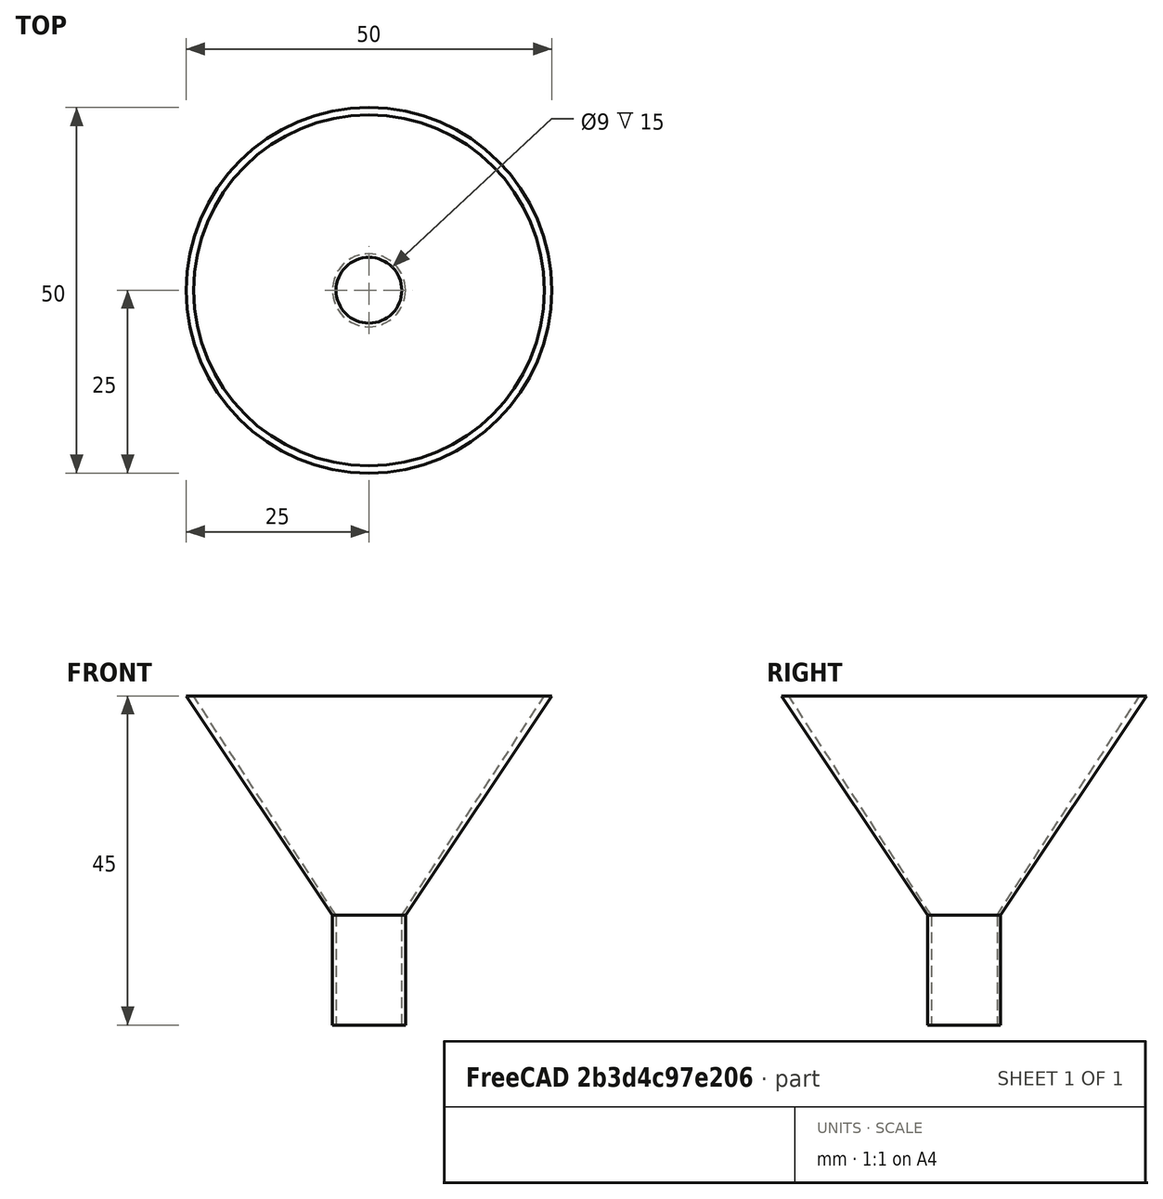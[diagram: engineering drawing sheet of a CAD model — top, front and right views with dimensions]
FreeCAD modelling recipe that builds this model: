
FCSTD DOCUMENT  (FreeCAD 1.0R39319 (Git))
Label: ojt1_t14r03_funnel
License: All rights reserved
LicenseURL: https://en.wikipedia.org/wiki/All_rights_reserved
objects: Part::Cylinder×2, Part::Cut×2, Part::Cone×2, Part::MultiFuse×1
note: 7 computed .brp shape members not serialized (recipe doc carries the construction recipe); baked Part::Feature solids carry a one-line shape summary decoded from their .brp

FEATURE [Part::Cylinder] Cylinder  label="Cilindre"
  Angle = 360
  AttacherType = Attacher::AttachEngine3D
  FirstAngle = 0
  Height = 15
  Radius = 5
  SecondAngle = 0
FEATURE [Part::Cylinder] Cylinder001  label="Cilindre001"
  Angle = 360
  AttacherType = Attacher::AttachEngine3D
  FirstAngle = 0
  Height = 15
  Radius = 4.5
  SecondAngle = 0
FEATURE [Part::Cut] Cut
  Base = -> Cylinder
  Refine = true
  Tool = -> Cylinder001
FEATURE [Part::Cone] Cone  label="Con"
  Angle = 360
  AttacherType = Attacher::AttachEngine3D
  Height = 30
  Placement = pos=(0,0,15) rot=(0,0,1;0rad)
  Radius1 = 5
  Radius2 = 25
FEATURE [Part::Cone] Cone001  label="Con001"
  Angle = 360
  AttacherType = Attacher::AttachEngine3D
  Height = 30
  Placement = pos=(0,0,15) rot=(0,0,1;0rad)
  Radius1 = 4.5
  Radius2 = 24
FEATURE [Part::Cut] Cut001
  Base = -> Cone
  Refine = true
  Tool = -> Cone001
FEATURE [Part::MultiFuse] Fusion
  Refine = true
  Shapes = -> [Cut001,Cut]
